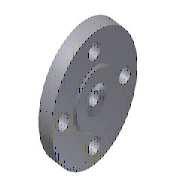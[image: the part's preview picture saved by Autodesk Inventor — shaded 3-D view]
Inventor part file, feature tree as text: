
AUTODESK INVENTOR PART (.ipt)
format: ipt  version: 2023.2 (Build 272271030, 271C)  size: 217,088 bytes
history: native  units: mm
features: sketch x2, revolve x1, extrude x1, pattern_circular x1
ambient origin geometry x8: Origin, YZ Plane, XZ Plane, XY Plane, X Axis, Y Axis, Z Axis, Center Point
bodies: Solid1 (feature_tree)
feature tree (5):
  revolve  "Revolution1"  [1 undecoded]
  extrude  "Extrusion1"  Depth=115.0mm
  pattern_circular  "Circular Pattern1"  Count=40  [1 undecoded]
  sketch  "Sketch1"  dims[d0=45.0mm d1=470.0mm]
  sketch  "Sketch2"  dims[d23=90.0deg d2=36.0mm d3=400.0mm d24=10.0mm d4=0.0mm d5=120.0mm d6=360.0deg d7=246.0mm d8=345.0mm d9=316.0mm d10=135.0deg d11=3.0mm d19=19.0mm d12=47.5mm d13=278.0mm d14=115.0mm d15=30.0deg d16=1.0mm d17=3.577925mm d18=298.0mm]
note: 2 required parameter values undecoded (feature->parameter linkage not recoverable at this tier; creation-order binding heuristic only, values carry confidence <= 0.55)